# Revit family: QF_MOFFAT_PFEN051--
name_source: partatom
category: Specialty Equipment
units: mm (PartAtom-declared; Revit-internal decimal feet)

## family parameters
Always vertical = Yes
Cut with Voids When Loaded = No
OmniClass Number = 23.40.40.14
OmniClass Title = Food Service Equipment
Part Type = Normal
Room Calculation Point = No
Round Connector Dimension = Use Diameter
Shared = No
Work Plane-Based = No

## types (22) — shared parameters
Accessory = No
CE Approved = Yes
Case_Height = 603 mm
Clearance_Front = 715 mm  [stored 2.3458 ft]
Clearance_Rear = 500 mm  [stored 1.64042 ft]
Clearance_Side_LH = 50 mm  [stored 0.164042 ft]
Clearance_Side_RH = 50 mm  [stored 0.164042 ft]
Clearance_Upper = 500 mm  [stored 1.64042 ft]
Cold Water Connection Height = 102 mm
Cold Water Size = 20 mm
Depth Actual = 744 mm  [stored 2.44094 ft]
Description = Electric Combi Oven for bakery&pastry, 5 Trays 600x400
Direct Waste Connection Height = 95 mm  [stored 0.31168 ft]
Direct Waste Size = 40 mm
Elec Connection Height = 102 mm
Electric power = 7250 W
Electrical Remarks = electrical connection with terminal box
Exhaust Static Press = 0.0 Pa
Exhaust Vent Depth = 80 mm  [stored 0.262467 ft]
Exhaust Vent Height = 723 mm  [stored 2.37205 ft]
Exhaust Vent Width = 40 mm  [stored 0.131234 ft]
FL Amps = 11 A
Filtered Treated Water Connection Height = 102 mm
Filtered Treated Water Flow = 0.0 L/min
Filtered Treated Water Supply Size = 20 mm
Foodservice Equipment Identifier = Yes
Handle_Z = 330 mm
Height Actual = 723 mm  [stored 2.37205 ft]
Identify Quantity as Lot = No
Item Number = PFEN051
Keynote = 0
Leg_R1 = 30 mm  [stored 0.0984252 ft]
Leg_R2 = 32.5 mm  [stored 0.106627 ft]
Leg_R3 = 40 mm  [stored 0.131234 ft]
Legs Height = 120 mm  [stored 0.393701 ft]
Length Actual = 777 mm  [stored 2.54921 ft]
Main switch integrated = No
Manufacturer = MOFFAT
Mat_Case = QF_Stainless-Brushed
Mat_Clearance = QF_Clearance
Mat_Glass = QF_Glass-Tempered-Clear
Mat_Handle = QF_Plastic-Black-Matte
Mat_Legs = QF_Stainless-Brushed
Mat_Plastic-Black = QF_Plastic-Black-Glossy
Model = PFEN051
Potential Equalisation = No
R2 = 2 mm  [stored 0.00656168 ft]
R6 = 6 mm  [stored 0.019685 ft]
URL Cutsheet = PFEN044_0124_en.pdf
URL Manufacturer = https://www.moffat.com
Volt Free Conn = No
Weight = 74.00 kg

## per-type parameters (varying)
| type | Cycle | DX_ | Left hinged | Logo_X | Number of Poles | Phase | Right hinged | SX_ | Volts |
| PFEN051 (230V 1NPh 50Hz) - LH | 50 Hz | 20 mm  [stored 0.0656168 ft] | Yes | 680 mm  [stored 2.23097 ft] | 1 | 1 | No | 0 mm  [stored 0 ft] | 230 V |
| PFEN051 (230V 1NPh 50Hz) - RH | 50 Hz | 0 mm  [stored 0 ft] | No | 90 mm  [stored 0.295276 ft] | 1 | 1 | Yes | 20 mm  [stored 0.0656168 ft] | 230 V |
| PFEN051 (230V 3Ph 50Hz) - LH | 50 Hz | 20 mm  [stored 0.0656168 ft] | Yes | 680 mm  [stored 2.23097 ft] | 3 | 3 | No | 0 mm  [stored 0 ft] | 230 V |
| PFEN051 (230V 3Ph 50Hz) - RH | 50 Hz | 0 mm  [stored 0 ft] | No | 90 mm  [stored 0.295276 ft] | 3 | 3 | Yes | 20 mm  [stored 0.0656168 ft] | 230 V |
| PFEN051 (400V 3NPh 50Hz) - LH | 50 Hz | 20 mm  [stored 0.0656168 ft] | Yes | 680 mm  [stored 2.23097 ft] | 3 | 3 | No | 0 mm  [stored 0 ft] | 400 V |
| PFEN051 (400V 3NPh 50Hz) - RH | 50 Hz | 0 mm  [stored 0 ft] | No | 90 mm  [stored 0.295276 ft] | 3 | 3 | Yes | 20 mm  [stored 0.0656168 ft] | 400 V |
| PFEN051 (400V 3Ph 50Hz) - LH | 50 Hz | 20 mm  [stored 0.0656168 ft] | Yes | 680 mm  [stored 2.23097 ft] | 3 | 3 | No | 0 mm  [stored 0 ft] | 400 V |
| PFEN051 (400V 3Ph 50Hz) - RH | 50 Hz | 0 mm  [stored 0 ft] | No | 90 mm  [stored 0.295276 ft] | 3 | 3 | Yes | 20 mm  [stored 0.0656168 ft] | 400 V |
| PFEN051 (400V 3Ph 60Hz) - LH | 60 Hz | 20 mm  [stored 0.0656168 ft] | Yes | 680 mm  [stored 2.23097 ft] | 3 | 3 | No | 0 mm  [stored 0 ft] | 400 V |
| PFEN051 (400V 3Ph 60Hz) - RH | 60 Hz | 0 mm  [stored 0 ft] | No | 90 mm  [stored 0.295276 ft] | 3 | 3 | Yes | 20 mm  [stored 0.0656168 ft] | 400 V |
| PFEN051 (440V 3Ph 50Hz) - LH | 50 Hz | 20 mm  [stored 0.0656168 ft] | Yes | 680 mm  [stored 2.23097 ft] | 3 | 3 | No | 0 mm  [stored 0 ft] | 440 V |
| PFEN051 (440V 3Ph 50Hz) - RH | 50 Hz | 0 mm  [stored 0 ft] | No | 90 mm  [stored 0.295276 ft] | 3 | 3 | Yes | 20 mm  [stored 0.0656168 ft] | 440 V |
| PFEN051 (440V 3Ph 60Hz) - LH | 60 Hz | 20 mm  [stored 0.0656168 ft] | Yes | 680 mm  [stored 2.23097 ft] | 3 | 3 | No | 0 mm  [stored 0 ft] | 440 V |
| PFEN051 (440V 3Ph 60Hz) - RH | 60 Hz | 0 mm  [stored 0 ft] | No | 90 mm  [stored 0.295276 ft] | 3 | 3 | Yes | 20 mm  [stored 0.0656168 ft] | 440 V |
| PFEN051 (440V 3NPh 50Hz) - LH | 50 Hz | 20 mm  [stored 0.0656168 ft] | Yes | 680 mm  [stored 2.23097 ft] | 3 | 3 | No | 0 mm  [stored 0 ft] | 440 V |
| PFEN051 (440V 3NPh 50Hz) - RH | 50 Hz | 0 mm  [stored 0 ft] | No | 90 mm  [stored 0.295276 ft] | 3 | 3 | Yes | 20 mm  [stored 0.0656168 ft] | 440 V |
| PFEN051 (440V 3NPh 60Hz) - LH | 60 Hz | 20 mm  [stored 0.0656168 ft] | Yes | 680 mm  [stored 2.23097 ft] | 3 | 3 | No | 0 mm  [stored 0 ft] | 440 V |
| PFEN051 (440V 3NPh 60Hz) - RH | 60 Hz | 0 mm  [stored 0 ft] | No | 90 mm  [stored 0.295276 ft] | 3 | 3 | Yes | 20 mm  [stored 0.0656168 ft] | 440 V |
| PFEN051 (480V 3Ph 50Hz) - LH | 50 Hz | 20 mm  [stored 0.0656168 ft] | Yes | 680 mm  [stored 2.23097 ft] | 3 | 3 | No | 0 mm  [stored 0 ft] | 480 V |
| PFEN051 (480V 3Ph 50Hz) - RH | 50 Hz | 0 mm  [stored 0 ft] | No | 90 mm  [stored 0.295276 ft] | 3 | 3 | Yes | 20 mm  [stored 0.0656168 ft] | 480 V |
| PFEN051 (480V 3Ph 60Hz) - LH | 60 Hz | 20 mm  [stored 0.0656168 ft] | Yes | 680 mm  [stored 2.23097 ft] | 3 | 3 | No | 0 mm  [stored 0 ft] | 480 V |
| PFEN051 (480V 3Ph 60Hz) - RH | 60 Hz | 0 mm  [stored 0 ft] | No | 90 mm  [stored 0.295276 ft] | 3 | 3 | Yes | 20 mm  [stored 0.0656168 ft] | 480 V |

note: [stored X ft] marks values corroborated as IEEE doubles in the binary element streams (Revit-internal decimal feet)

## geometry (parser evidence)
native form markers: Sweep x22
no freeform markers — native parametric forms only
